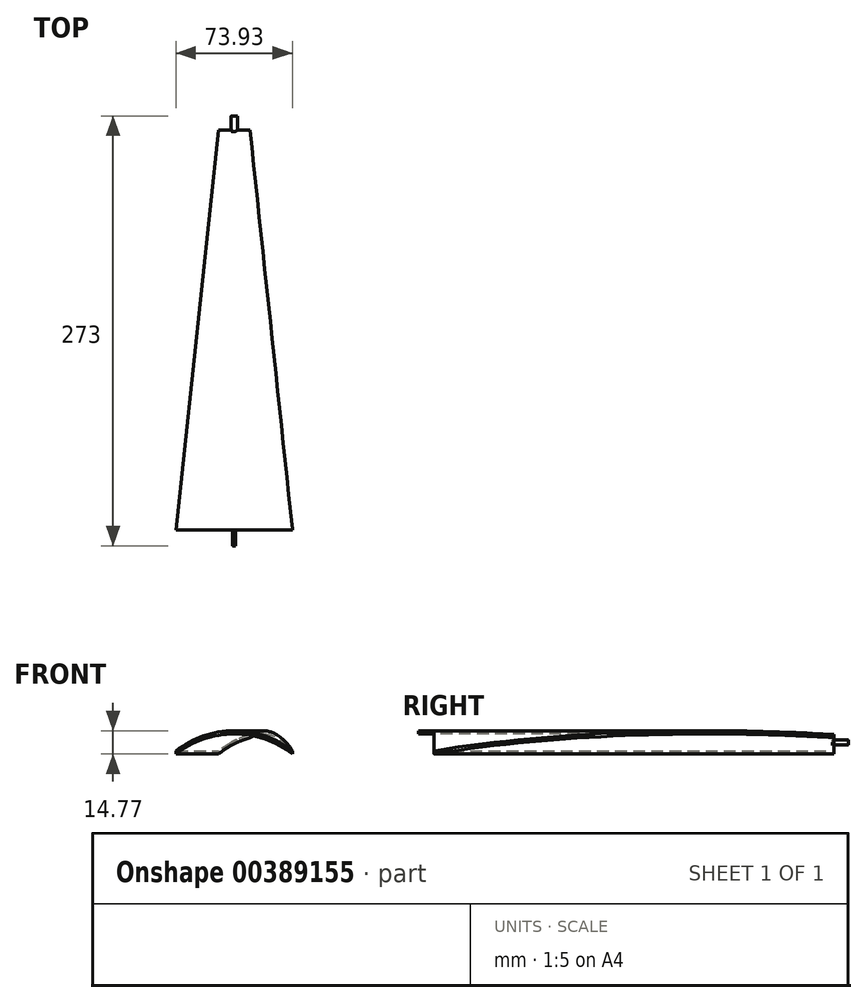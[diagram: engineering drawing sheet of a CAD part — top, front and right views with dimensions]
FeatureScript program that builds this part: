
annotation { "Feature Type Name" : "Feature", "Feature Type Description" : "" }
export const myFeature = defineFeature(function(context is Context, id is Id, definition is map)
    precondition{}
    {
        {
            var Q0;
            Q0=qCreatedBy(makeId("Top.planeOp"),FACE);
            var sketch = newSketch(context, id + "F0", { "sketchPlane" : qUnion([Q0])});
            skLineSegment(sketch, "E0", {"start": v(0, -66.65) * mm, "end": v(-2, -66.65) * mm});
            skLineSegment(sketch, "E1", {"start": v(-2, -66.65) * mm, "end": v(-2, -56.65) * mm});
            skLineSegment(sketch, "E2", {"start": v(-2, -56.65) * mm, "end": v(-37, -56.65) * mm});
            skLineSegment(sketch, "E3", {"start": v(-37, -56.65) * mm, "end": v(-10, 197.35) * mm});
            skLineSegment(sketch, "E4", {"start": v(-10, 197.35) * mm, "end": v(-2, 197.35) * mm});
            skLineSegment(sketch, "E5", {"start": v(-2, 197.35) * mm, "end": v(-2, 207.35) * mm});
            skLineSegment(sketch, "E6", {"start": v(-2, 207.35) * mm, "end": v(0, 207.35) * mm});
            skLineSegment(sketch, "E7.MirrorCS", {"start": v(10, 197.35) * mm, "end": v(2, 197.35) * mm});
            skLineSegment(sketch, "E8.MirrorCS", {"start": v(2, 207.35) * mm, "end": v(0, 207.35) * mm});
            skLineSegment(sketch, "E9.MirrorCS", {"start": v(0, -66.65) * mm, "end": v(2, -66.65) * mm});
            skLineSegment(sketch, "E10.MirrorCS", {"start": v(2, -66.65) * mm, "end": v(2, -56.65) * mm});
            skLineSegment(sketch, "E11.MirrorCS", {"start": v(2, 197.35) * mm, "end": v(2, 207.35) * mm});
            skLineSegment(sketch, "E12.MirrorCS", {"start": v(2, -56.65) * mm, "end": v(37, -56.65) * mm});
            skLineSegment(sketch, "E13.MirrorCS", {"start": v(37, -56.65) * mm, "end": v(10, 197.35) * mm});
            skLineSegment(sketch, "E14", {"start": v(-2, -56.65) * mm, "end": v(2, -56.65) * mm});
            skLineSegment(sketch, "E15", {"start": v(-2, 197.35) * mm, "end": v(-2, 196.35) * mm});
            skLineSegment(sketch, "E16", {"start": v(-2, 196.35) * mm, "end": v(2, 196.35) * mm});
            skLineSegment(sketch, "E17", {"start": v(2, 196.35) * mm, "end": v(2, 197.35) * mm});
            skSolve(sketch);
        }
        {
            var Q0;
            Q0=makeQuery(id+"F0.imprint","IMPRINT",FACE,{"disambiguationData":[TD([[makeQuery(id+"F0.imprint","IMPRINT",EDGE,{"derivedFrom":sQuery(id+"F0.wireOp",EDGE,"E2")}),-1.0]])]});
            extrude(context, id + "F1", {"entities" : qUnion([Q0]), "depth" : 25 * mm});
        }
        {
            var Q0;
            Q0=makeQuery(id+"F1.opExtrude","SWEPT_FACE",FACE,{"disambiguationData":[OSD([sQuery(id+"F0.wireOp",EDGE,"E2")])]});
            var sketch = newSketch(context, id + "F2", { "sketchPlane" : qUnion([Q0])});
            skLineSegment(sketch, "E18", {"start": v(36.87, 0) * mm, "end": v(36.87, 2) * mm});
            skLineSegment(sketch, "E19", {"start": v(-37, 0) * mm, "end": v(-37, 2) * mm});
            skArc(sketch, "E20", {"start": v(36.87, 2) * mm, "mid": v(-0.07, 14.71) * mm, "end": v(-37, 2) * mm});
            skArc(sketch, "E21", {"start": v(37, 0) * mm, "mid": v(0, 12.77) * mm, "end": v(-37, 0) * mm});
            skSolve(sketch);
        }
        {
            var Q0;
            Q0 = qSketchRegion(id + "F2", true);
            var Q1;
            Q1 = qConstructionFilter(qBodyType(qCreatedBy(id + "F2" ,EDGE), BodyType.WIRE), ConstructionObject.NO);
            var Q2;
            Q2=makeQuery(id+"F1.opExtrude","CAP_EDGE",EDGE,{"disambiguationData":[OSD([sQuery(id+"F0.wireOp",EDGE,"E3")])],"isStart":true});
            sweep(context, id + "F3", {"operationType" : NewBodyOperationType.INTERSECT, "profiles" : qUnion([Q0]), "surfaceProfiles" : qUnion([Q1]), "path" : qUnion([Q2])});
        }
        {
            var Q0;
            Q0=makeQuery(id+"F1.opExtrude","SWEPT_FACE",FACE,{"disambiguationData":[OSD([sQuery(id+"F0.wireOp",EDGE,"E16")])]});
            extrude(context, id + "F4", {"entities" : qUnion([Q0]), "operationType" : NewBodyOperationType.ADD, "depth" : 10 * mm});
        }
        {
            var Q0;
            Q0=makeQuery(id+"F4.opExtrude","SWEPT_EDGE",EDGE,{"disambiguationData":[OSD([sQuery(id+"F0.wireOp",EDGE,"E3"),sQuery(id+"F0.wireOp",EDGE,"E16"),sQuery(id+"F0.wireOp",EDGE,"E17"),sQuery(id+"F2.wireOp",EDGE,"E20")])]});
            var Q1;
            {var subQ0=sQuery(id+"F0.wireOp",EDGE,"E17");var subQ1=sQuery(id+"F0.wireOp",EDGE,"E16");var subQ2=sQuery(id+"F2.wireOp",EDGE,"E21");var subQ3=sQuery(id+"F0.wireOp",EDGE,"E3");Q1=makeQuery(id+"F4.boolean.opBoolean","SPLIT",EDGE,{"disambiguationData":[topologyDisambiguationEdgeConnected([makeQuery(id+"F4.opExtrude","SWEPT_FACE",FACE,{"disambiguationData":[OSD([subQ1,subQ0])]})])],"derivedFrom":makeQuery(id+"F4.opExtrude","SWEPT_EDGE",EDGE,{"disambiguationData":[OSD([subQ3,subQ1,subQ0,subQ2])]})});}
            var Q2;
            Q2=makeQuery(id+"F4.opExtrude","SWEPT_EDGE",EDGE,{"disambiguationData":[OSD([sQuery(id+"F0.wireOp",EDGE,"E3"),sQuery(id+"F0.wireOp",EDGE,"E15"),sQuery(id+"F0.wireOp",EDGE,"E16"),sQuery(id+"F2.wireOp",EDGE,"E20")])]});
            var Q3;
            {var subQ0=sQuery(id+"F0.wireOp",EDGE,"E16");var subQ1=sQuery(id+"F0.wireOp",EDGE,"E15");var subQ2=sQuery(id+"F2.wireOp",EDGE,"E21");var subQ3=sQuery(id+"F0.wireOp",EDGE,"E3");Q3=makeQuery(id+"F4.boolean.opBoolean","SPLIT",EDGE,{"disambiguationData":[topologyDisambiguationEdgeConnected([makeQuery(id+"F4.opExtrude","SWEPT_FACE",FACE,{"disambiguationData":[OSD([subQ1,subQ0])]})])],"derivedFrom":makeQuery(id+"F4.opExtrude","SWEPT_EDGE",EDGE,{"disambiguationData":[OSD([subQ3,subQ1,subQ0,subQ2])]})});}
            fillet(context, id + "F5", {"entities" : qUnion([Q0, Q1, Q2, Q3]), "radius" : 0.8 * mm, "tangentPropagation" : true, "allowEdgeOverflow" : false});
        }
        {
            var Q0;
            Q0=makeQuery(id+"F1.opExtrude","SWEPT_FACE",FACE,{"disambiguationData":[OSD([sQuery(id+"F0.wireOp",EDGE,"E2"),sQuery(id+"F0.wireOp",EDGE,"E12.MirrorCS"),sQuery(id+"F0.wireOp",EDGE,"E14")])]});
            var sketch = newSketch(context, id + "F6", { "sketchPlane" : qUnion([Q0])});
            skCircle(sketch, "E22", {"center": v(0, 13.78) * mm, "radius": 0.98 * mm});
            skSolve(sketch);
        }
        {
            var Q0;
            Q0 = qSketchRegion(id + "F6", true);
            extrude(context, id + "F7", {"entities" : qUnion([Q0]), "operationType" : NewBodyOperationType.ADD, "depth" : 10 * mm});
        }
    });
